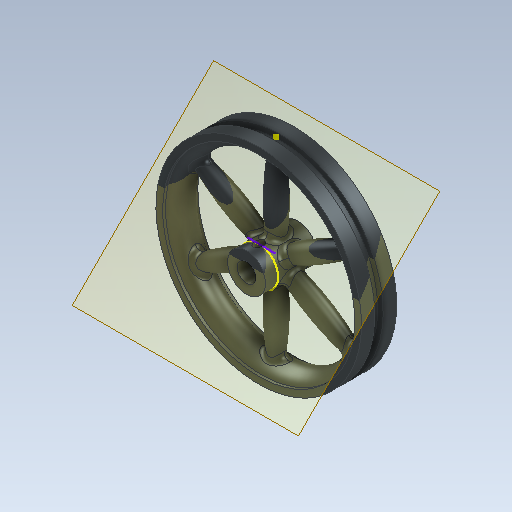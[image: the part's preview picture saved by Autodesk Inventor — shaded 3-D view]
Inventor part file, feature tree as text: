
AUTODESK INVENTOR PART (.ipt)
format: ipt  version: 2020 (Build 240168000, 168)  size: 697,344 bytes
history: native  units: mm
features: sketch x7, revolve x2, extrude x2, pattern_circular x1, fillet x1, hole x1, plane x1, thread x1, projected_geometry x1
ambient origin geometry x8: Origin, YZ Plane, XZ Plane, XY Plane, X Axis, Y Axis, Z Axis, Center Point
bodies: Solid1 (feature_tree)
feature tree (17):
  revolve  "Revolution1"  [1 undecoded]
  sketch  "Sketch2"  dims[d2=6.5mm d3=38.0mm]
  extrude  "Extrusion1"  Depth=38.0mm
  revolve  "Revolution2"  [1 undecoded]
  pattern_circular  "Circular Pattern1"  [2 undecoded]
  fillet  "Fillet1"  Radius=14.0mm
  hole  "Hole1"  [1 undecoded]
  sketch  "Sketch6"  dims[d8=5.0mm]
  plane  "Work Plane1"
  extrude  "Extrusion2"  Depth=3.0mm
  thread  "Thread1"  [1 undecoded]
  sketch  "Sketch1"  dims[d0=2.5mm d1=13.0mm]
  sketch  "Sketch3"  dims[d4=12.0mm d5=2.0mm]
  sketch  "Sketch4"  dims[d6=3.0mm]
  sketch  "Sketch5"  dims[d7=90.0deg]
  projected_geometry  "Projected Loop1"
  sketch  "Sketch7"  dims[d9=2.5mm d10=0.0mm d11=14.0mm d12=11.0mm d13=8.0mm d14=0.0mm d15=0.0mm d16=3.0mm d17=100.0mm d18=90.0deg d19=6.9mm d20=60.0mm d21=360.0deg d23=2.0mm d24=7.0mm d25=6.0mm d26=4.0mm d27=2.0mm d28=90.0deg d29=7.0mm d30=20.594885mm d31=45.0deg d32=3.0mm d33=2.0mm d34=8.28mm d35=0.0mm d36=0.0mm d37=7.95mm d38=0.0mm d39=0.75mm d40=20.594885mm d41=0.0625mm d42=0.75mm d43=0.375mm]
note: 6 required parameter values undecoded (feature->parameter linkage not recoverable at this tier; creation-order binding heuristic only, values carry confidence <= 0.55)